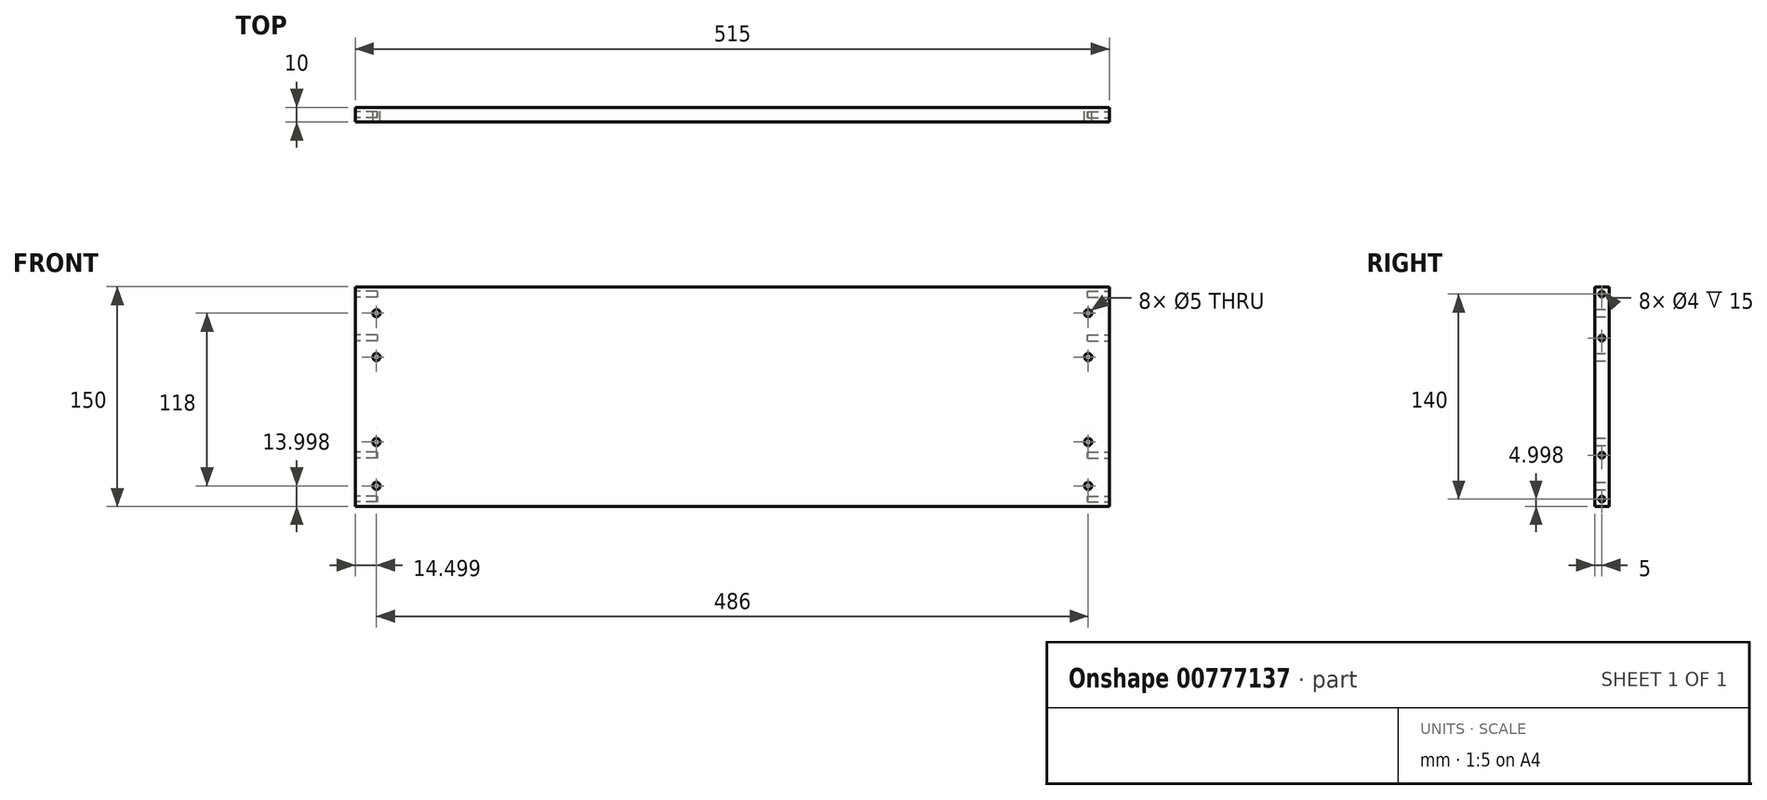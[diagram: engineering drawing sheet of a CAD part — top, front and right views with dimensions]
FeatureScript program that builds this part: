
annotation { "Feature Type Name" : "Feature", "Feature Type Description" : "" }
export const myFeature = defineFeature(function(context is Context, id is Id, definition is map)
    precondition{}
    {
        {
            var Q0;
            Q0=qCreatedBy(makeId("Front.planeOp"),FACE);
            var sketch = newSketch(context, id + "F0", { "sketchPlane" : qUnion([Q0])});
            skLineSegment(sketch, "E0.bottom", {"start": v(-255.67, 131.67) * mm, "end": v(259.33, 131.67) * mm});
            skLineSegment(sketch, "E0.top", {"start": v(-255.67, -18.33) * mm, "end": v(259.33, -18.33) * mm});
            skLineSegment(sketch, "E0.left", {"start": v(-255.67, 131.67) * mm, "end": v(-255.67, -18.33) * mm});
            skLineSegment(sketch, "E0.right", {"start": v(259.33, 131.67) * mm, "end": v(259.33, -18.33) * mm});
            skCircle(sketch, "E1", {"center": v(244.83, 113.67) * mm, "radius": 2.5 * mm});
            skCircle(sketch, "E2", {"center": v(244.83, 83.67) * mm, "radius": 2.5 * mm});
            skCircle(sketch, "E3", {"center": v(244.83, 25.67) * mm, "radius": 2.5 * mm});
            skCircle(sketch, "E4", {"center": v(244.83, -4.33) * mm, "radius": 2.5 * mm});
            skCircle(sketch, "E5", {"center": v(-241.17, -4.33) * mm, "radius": 2.5 * mm});
            skCircle(sketch, "E6", {"center": v(-241.17, 25.67) * mm, "radius": 2.5 * mm});
            skCircle(sketch, "E7", {"center": v(-241.17, 83.67) * mm, "radius": 2.5 * mm});
            skCircle(sketch, "E8", {"center": v(-241.17, 113.67) * mm, "radius": 2.5 * mm});
            skSolve(sketch);
        }
        {
            var Q0;
            Q0=makeQuery(id+"F0.imprint","IMPRINT",FACE,{"disambiguationData":[TD([[makeQuery(id+"F0.imprint","IMPRINT",EDGE,{"derivedFrom":sQuery(id+"F0.wireOp",EDGE,"E0.bottom")}),-1.0]])]});
            extrude(context, id + "F1", {"entities" : qUnion([Q0]), "depth" : 10 * mm, "offsetDistance" : 25 * mm});
        }
        {
            var Q0;
            Q0=makeQuery(id+"F1.opExtrude","SWEPT_FACE",FACE,{"disambiguationData":[OSD([sQuery(id+"F0.wireOp",EDGE,"E0.left")])]});
            var sketch = newSketch(context, id + "F2", { "sketchPlane" : qUnion([Q0])});
            skCircle(sketch, "E9", {"center": v(5, 126.67) * mm, "radius": 2 * mm});
            skPoint(sketch, "E9.centerSnap0", {"position": v(5, 131.67) * mm});
            skCircle(sketch, "E10", {"center": v(5, 96.67) * mm, "radius": 2 * mm});
            skCircle(sketch, "E11", {"center": v(5, -13.33) * mm, "radius": 2 * mm});
            skCircle(sketch, "E12", {"center": v(5, 16.67) * mm, "radius": 2 * mm});
            skSolve(sketch);
        }
        {
            var Q0;
            Q0=makeQuery(id+"F2.imprint","IMPRINT",FACE,{"disambiguationData":[TD([[makeQuery(id+"F2.imprint","IMPRINT",EDGE,{"derivedFrom":sQuery(id+"F2.wireOp",EDGE,"E11")}),1.0]])]});
            var Q1;
            Q1=makeQuery(id+"F2.imprint","IMPRINT",FACE,{"disambiguationData":[TD([[makeQuery(id+"F2.imprint","IMPRINT",EDGE,{"derivedFrom":sQuery(id+"F2.wireOp",EDGE,"E9")}),1.0]])]});
            var Q2;
            Q2=makeQuery(id+"F2.imprint","IMPRINT",FACE,{"disambiguationData":[TD([[makeQuery(id+"F2.imprint","IMPRINT",EDGE,{"derivedFrom":sQuery(id+"F2.wireOp",EDGE,"E10")}),1.0]])]});
            var Q3;
            Q3=makeQuery(id+"F2.imprint","IMPRINT",FACE,{"disambiguationData":[TD([[makeQuery(id+"F2.imprint","IMPRINT",EDGE,{"derivedFrom":sQuery(id+"F2.wireOp",EDGE,"E12")}),1.0]])]});
            extrude(context, id + "F3", {"entities" : qUnion([Q0, Q1, Q2, Q3]), "operationType" : NewBodyOperationType.REMOVE, "oppositeDirection" : true, "depth" : 15 * mm, "offsetDistance" : 25 * mm});
        }
        {
            var Q0;
            Q0=makeQuery(id+"F1.opExtrude","SWEPT_FACE",FACE,{"disambiguationData":[OSD([sQuery(id+"F0.wireOp",EDGE,"E0.right")])]});
            var sketch = newSketch(context, id + "F4", { "sketchPlane" : qUnion([Q0])});
            skCircle(sketch, "E13", {"center": v(-5, 126.67) * mm, "radius": 2 * mm});
            skPoint(sketch, "E13.centerSnap0", {"position": v(-5, 131.67) * mm});
            skCircle(sketch, "E14", {"center": v(-5, 96.67) * mm, "radius": 2 * mm});
            skCircle(sketch, "E15", {"center": v(-5, -13.33) * mm, "radius": 2 * mm});
            skCircle(sketch, "E16", {"center": v(-5, 16.67) * mm, "radius": 2 * mm});
            skSolve(sketch);
        }
        {
            var Q0;
            Q0=makeQuery(id+"F4.imprint","IMPRINT",FACE,{"disambiguationData":[TD([[makeQuery(id+"F4.imprint","IMPRINT",EDGE,{"derivedFrom":sQuery(id+"F4.wireOp",EDGE,"E14")}),1.0]])]});
            var Q1;
            Q1=makeQuery(id+"F4.imprint","IMPRINT",FACE,{"disambiguationData":[TD([[makeQuery(id+"F4.imprint","IMPRINT",EDGE,{"derivedFrom":sQuery(id+"F4.wireOp",EDGE,"E15")}),1.0]])]});
            var Q2;
            Q2=makeQuery(id+"F4.imprint","IMPRINT",FACE,{"disambiguationData":[TD([[makeQuery(id+"F4.imprint","IMPRINT",EDGE,{"derivedFrom":sQuery(id+"F4.wireOp",EDGE,"E13")}),1.0]])]});
            var Q3;
            Q3=makeQuery(id+"F4.imprint","IMPRINT",FACE,{"disambiguationData":[TD([[makeQuery(id+"F4.imprint","IMPRINT",EDGE,{"derivedFrom":sQuery(id+"F4.wireOp",EDGE,"E16")}),1.0]])]});
            extrude(context, id + "F5", {"entities" : qUnion([Q0, Q1, Q2, Q3]), "operationType" : NewBodyOperationType.REMOVE, "oppositeDirection" : true, "depth" : 15 * mm, "offsetDistance" : 25 * mm});
        }
    });
